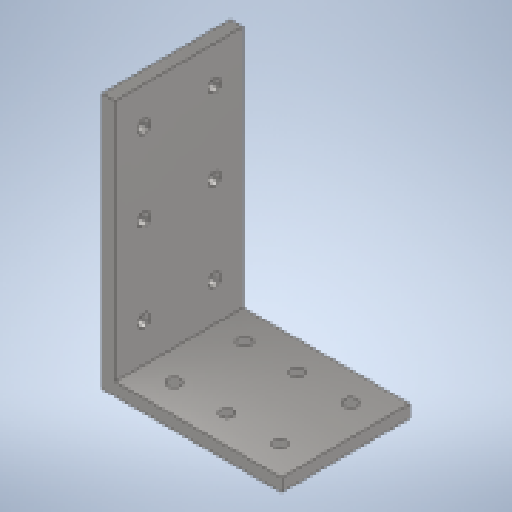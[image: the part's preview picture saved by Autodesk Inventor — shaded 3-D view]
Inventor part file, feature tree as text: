
AUTODESK INVENTOR PART (.ipt)
format: ipt  version: 2025.2 (Build 292293000, 293)  size: 277,504 bytes
history: native  units: in
note: dims shown in document units (in); Inventor stores cm internally (conversion verified against a paired STEP export)
features: extrude x3, sketch x2
ambient origin geometry x8: Origin, YZ Plane, XZ Plane, XY Plane, X Axis, Y Axis, Z Axis, Center Point
bodies: Solid1 (feature_tree)
feature tree (5):
  extrude  "Extrusion1"  Depth=5.0in
  extrude  "Extrusion2"  Depth=2.5in TaperAngle=0.0deg
  extrude  "Extrusion3"  Depth=0.25in
  sketch  "Sketch1"  dims[d0=3.5in d1=5.0in]
  sketch  "Sketch3"  dims[d2=0.25in d3=2.5in d4=0.0in d5=0.25in d6=0.25in d7=2.5in d9=3.5in d10=0.5906in d12=0.0in d13=0.0in d14=1.378in d15=1.5748in d16=1.5in d17=0.25in d18=0.0in d19=0.0in d20=4.0in d21=1.378in]
